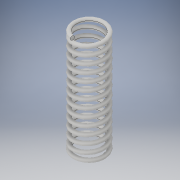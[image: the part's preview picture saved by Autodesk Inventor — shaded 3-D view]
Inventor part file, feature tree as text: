
AUTODESK INVENTOR PART (.ipt)
format: ipt  version: 2018 (Build 220112000, 112)  size: 422,912 bytes
history: native  units: in
note: dims shown in document units (in); Inventor stores cm internally (conversion verified against a paired STEP export)
features: helix x1, sketch x1
ambient origin geometry x8: Origin, YZ Plane, XZ Plane, XY Plane, X Axis, Y Axis, Z Axis, Center Point
bodies: Solid1 (feature_tree)
feature tree (2):
  helix  "Coil1"  [1 undecoded]
  sketch  "Sketch1"  dims[d1=0.0875in d2=1.0in d3=0.5381in d4=5.1181in d5=0.0in d6=90.0deg d7=0.8933in d8=90.0deg d9=0.8933in]
note: 1 required parameter value undecoded (feature->parameter linkage not recoverable at this tier; creation-order binding heuristic only, values carry confidence <= 0.55)
